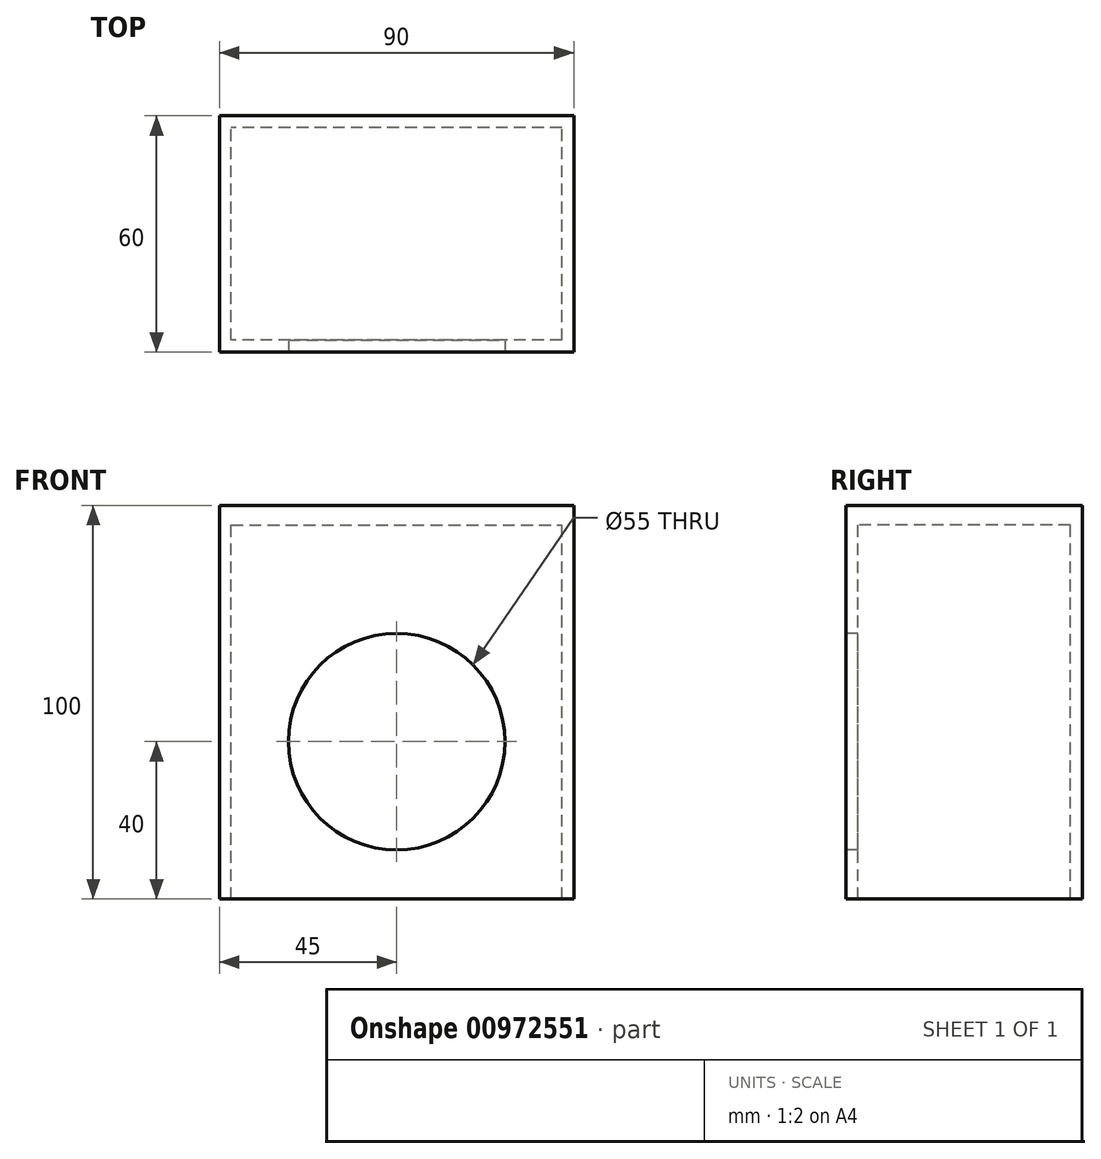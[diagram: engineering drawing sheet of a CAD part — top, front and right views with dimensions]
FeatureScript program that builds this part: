
annotation { "Feature Type Name" : "Feature", "Feature Type Description" : "" }
export const myFeature = defineFeature(function(context is Context, id is Id, definition is map)
    precondition{}
    {
        {
            var Q0;
            Q0=qCreatedBy(makeId("Top.planeOp"),FACE);
            var sketch = newSketch(context, id + "F0", { "sketchPlane" : qUnion([Q0])});
            skLineSegment(sketch, "E0.bottom", {"start": v(0, 0) * mm, "end": v(90, 0) * mm});
            skLineSegment(sketch, "E0.top", {"start": v(0, -60) * mm, "end": v(90, -60) * mm});
            skLineSegment(sketch, "E0.left", {"start": v(0, 0) * mm, "end": v(0, -60) * mm});
            skLineSegment(sketch, "E0.right", {"start": v(90, 0) * mm, "end": v(90, -60) * mm});
            skSolve(sketch);
        }
        {
            var Q0;
            Q0 = qSketchRegion(id + "F0", true);
            extrude(context, id + "F1", {"entities" : qUnion([Q0]), "depth" : 100 * mm, "offsetDistance" : 25 * mm});
        }
        {
            var Q0;
            Q0=makeQuery(id+"F1.opExtrude","CAP_FACE",FACE,{"disambiguationData":[OSD([sQuery(id+"F0.wireOp",EDGE,"E0.bottom"),sQuery(id+"F0.wireOp",EDGE,"E0.top"),sQuery(id+"F0.wireOp",EDGE,"E0.left"),sQuery(id+"F0.wireOp",EDGE,"E0.right")])],"isStart":false});
            cPlane(context, id + "F2", {"entities" : qUnion([Q0]), "cplaneType" : CPlaneType.OFFSET, "offset" : 5 * mm, "oppositeDirection" : true, "width" : 150 * mm, "height" : 150 * mm});
        }
        {
            var Q0;
            Q0=qCreatedBy(id+"F2.planeOp",FACE);
            var sketch = newSketch(context, id + "F3", { "sketchPlane" : qUnion([Q0])});
            skLineSegment(sketch, "E1.bottom", {"start": v(3, -3) * mm, "end": v(87, -3) * mm});
            skLineSegment(sketch, "E1.top", {"start": v(3, -57) * mm, "end": v(87, -57) * mm});
            skLineSegment(sketch, "E1.left", {"start": v(3, -3) * mm, "end": v(3, -57) * mm});
            skLineSegment(sketch, "E1.right", {"start": v(87, -3) * mm, "end": v(87, -57) * mm});
            skSolve(sketch);
        }
        {
            var Q0;
            Q0 = qSketchRegion(id + "F3", true);
            var Q1;
            Q1=makeQuery(id+"F1.opExtrude","CAP_FACE",FACE,{"disambiguationData":[OSD([sQuery(id+"F0.wireOp",EDGE,"E0.bottom"),sQuery(id+"F0.wireOp",EDGE,"E0.top"),sQuery(id+"F0.wireOp",EDGE,"E0.left"),sQuery(id+"F0.wireOp",EDGE,"E0.right")])],"isStart":true});
            extrude(context, id + "F4", {"entities" : qUnion([Q0]), "operationType" : NewBodyOperationType.REMOVE, "endBound" : BoundingType.UP_TO_SURFACE, "oppositeDirection" : true, "depth" : 25 * mm, "endBoundEntityFace" : qUnion([Q1]), "offsetDistance" : 3 * mm});
        }
        {
            var Q0;
            Q0=makeQuery(id+"F1.opExtrude","SWEPT_FACE",FACE,{"disambiguationData":[OSD([sQuery(id+"F0.wireOp",EDGE,"E0.top")])]});
            var sketch = newSketch(context, id + "F5", { "sketchPlane" : qUnion([Q0])});
            skLineSegment(sketch, "E2", {"start": v(45, 100) * mm, "end": v(45, 0) * mm, "construction": true});
            skCircle(sketch, "E3", {"center": v(45, 40) * mm, "radius": 27.5 * mm});
            skSolve(sketch);
        }
        {
            var Q0;
            Q0 = qSketchRegion(id + "F5", true);
            extrude(context, id + "F6", {"entities" : qUnion([Q0]), "operationType" : NewBodyOperationType.REMOVE, "endBound" : BoundingType.UP_TO_NEXT, "oppositeDirection" : true, "depth" : 25 * mm, "offsetDistance" : 25 * mm});
        }
    });
